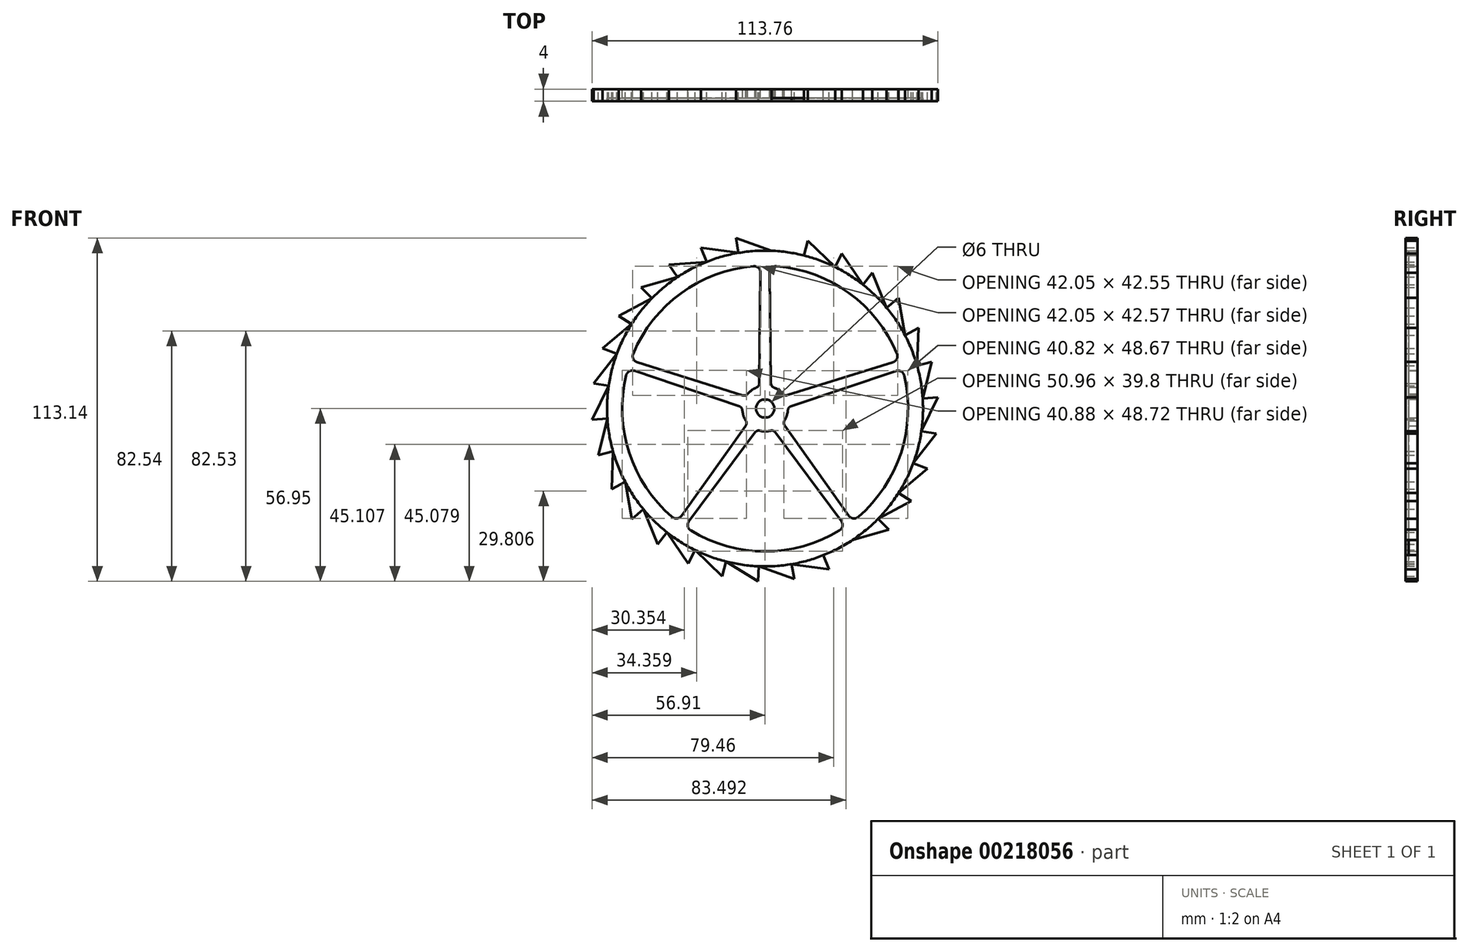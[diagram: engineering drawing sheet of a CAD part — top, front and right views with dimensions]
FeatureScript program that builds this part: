
annotation { "Feature Type Name" : "Feature", "Feature Type Description" : "" }
export const myFeature = defineFeature(function(context is Context, id is Id, definition is map)
    precondition{}
    {
        {
            var Q0;
            Q0=qCreatedBy(makeId("Front.planeOp"),FACE);
            var sketch = newSketch(context, id + "F0", { "sketchPlane" : qUnion([Q0])});
            skLineSegment(sketch, "E0", {"start": v(16.93, -54.43) * mm, "end": v(16.97, -54.42) * mm});
            skCircle(sketch, "E1", {"center": v(-0.03, 0) * mm, "radius": 52 * mm});
            skLineSegment(sketch, "E2", {"start": v(48.74, -18.05) * mm, "end": v(53.43, -19.79) * mm});
            skLineSegment(sketch, "E3", {"start": v(53.43, -19.79) * mm, "end": v(43.92, -27.8) * mm});
            skLineSegment(sketch, "E4.1.0", {"start": v(43.92, -27.8) * mm, "end": v(48.14, -30.47) * mm});
            skLineSegment(sketch, "E4.1.1", {"start": v(48.14, -30.47) * mm, "end": v(37.18, -36.33) * mm});
            skLineSegment(sketch, "E4.2.0", {"start": v(37.18, -36.33) * mm, "end": v(40.76, -39.82) * mm});
            skLineSegment(sketch, "E4.2.1", {"start": v(40.76, -39.82) * mm, "end": v(28.81, -43.27) * mm});
            skLineSegment(sketch, "E4.3.0", {"start": v(28.81, -43.27) * mm, "end": v(31.59, -47.43) * mm});
            skLineSegment(sketch, "E4.3.1", {"start": v(31.59, -47.43) * mm, "end": v(19.18, -48.32) * mm});
            skLineSegment(sketch, "E4.4.0", {"start": v(19.19, -48.32) * mm, "end": v(21.03, -52.96) * mm});
            skLineSegment(sketch, "E4.4.1", {"start": v(21.03, -52.96) * mm, "end": v(8.72, -51.26) * mm});
            skLineSegment(sketch, "E4.5.0", {"start": v(8.72, -51.26) * mm, "end": v(9.56, -56.19) * mm});
            skLineSegment(sketch, "E4.5.1", {"start": v(9.56, -56.19) * mm, "end": v(-2.13, -51.96) * mm});
            skLineSegment(sketch, "E4.6.0", {"start": v(-2.13, -51.96) * mm, "end": v(-2.33, -56.95) * mm});
            skLineSegment(sketch, "E4.6.1", {"start": v(-2.33, -56.95) * mm, "end": v(-12.89, -50.39) * mm});
            skLineSegment(sketch, "E4.7.0", {"start": v(-12.88, -50.39) * mm, "end": v(-14.12, -55.23) * mm});
            skLineSegment(sketch, "E4.7.1", {"start": v(-14.12, -55.23) * mm, "end": v(-23.08, -46.61) * mm});
            skLineSegment(sketch, "E4.8.0", {"start": v(-23.08, -46.61) * mm, "end": v(-25.3, -51.1) * mm});
            skLineSegment(sketch, "E4.8.1", {"start": v(-25.3, -51.1) * mm, "end": v(-32.27, -40.8) * mm});
            skLineSegment(sketch, "E4.9.0", {"start": v(-32.27, -40.8) * mm, "end": v(-35.37, -44.72) * mm});
            skLineSegment(sketch, "E4.9.1", {"start": v(-35.37, -44.72) * mm, "end": v(-40.05, -33.2) * mm});
            skLineSegment(sketch, "E4.10.0", {"start": v(-40.05, -33.2) * mm, "end": v(-43.9, -36.4) * mm});
            skLineSegment(sketch, "E4.10.1", {"start": v(-43.9, -36.4) * mm, "end": v(-46.08, -24.16) * mm});
            skLineSegment(sketch, "E4.11.0", {"start": v(-46.08, -24.16) * mm, "end": v(-50.5, -26.49) * mm});
            skLineSegment(sketch, "E4.11.1", {"start": v(-50.5, -26.49) * mm, "end": v(-50.1, -14.06) * mm});
            skLineSegment(sketch, "E4.12.0", {"start": v(-50.1, -14.06) * mm, "end": v(-54.9, -15.41) * mm});
            skLineSegment(sketch, "E4.12.1", {"start": v(-54.9, -15.41) * mm, "end": v(-51.92, -3.34) * mm});
            skLineSegment(sketch, "E4.13.0", {"start": v(-51.92, -3.34) * mm, "end": v(-56.91, -3.67) * mm});
            skLineSegment(sketch, "E4.13.1", {"start": v(-56.91, -3.67) * mm, "end": v(-51.48, 7.52) * mm});
            skLineSegment(sketch, "E4.14.0", {"start": v(-51.48, 7.52) * mm, "end": v(-56.43, 8.24) * mm});
            skLineSegment(sketch, "E4.14.1", {"start": v(-56.43, 8.24) * mm, "end": v(-48.8, 18.05) * mm});
            skLineSegment(sketch, "E4.15.0", {"start": v(-48.8, 18.05) * mm, "end": v(-53.49, 19.79) * mm});
            skLineSegment(sketch, "E4.15.1", {"start": v(-53.49, 19.79) * mm, "end": v(-43.98, 27.8) * mm});
            skLineSegment(sketch, "E4.16.0", {"start": v(-43.98, 27.8) * mm, "end": v(-48.2, 30.47) * mm});
            skLineSegment(sketch, "E4.16.1", {"start": v(-48.2, 30.47) * mm, "end": v(-37.24, 36.33) * mm});
            skLineSegment(sketch, "E4.17.0", {"start": v(-37.24, 36.33) * mm, "end": v(-40.82, 39.82) * mm});
            skLineSegment(sketch, "E4.17.1", {"start": v(-40.82, 39.82) * mm, "end": v(-28.87, 43.27) * mm});
            skLineSegment(sketch, "E4.18.0", {"start": v(-28.87, 43.27) * mm, "end": v(-31.65, 47.43) * mm});
            skLineSegment(sketch, "E4.18.1", {"start": v(-31.65, 47.43) * mm, "end": v(-19.24, 48.32) * mm});
            skLineSegment(sketch, "E4.19.0", {"start": v(-19.25, 48.32) * mm, "end": v(-21.1, 52.96) * mm});
            skLineSegment(sketch, "E4.19.1", {"start": v(-21.1, 52.96) * mm, "end": v(-8.78, 51.26) * mm});
            skLineSegment(sketch, "E4.20.0", {"start": v(-8.78, 51.26) * mm, "end": v(-9.62, 56.19) * mm});
            skLineSegment(sketch, "E4.20.1", {"start": v(-9.62, 56.19) * mm, "end": v(2.07, 51.96) * mm});
            skLineSegment(sketch, "E4.21.0", {"start": v(2.07, 51.96) * mm, "end": v(2.27, 56.95) * mm});
            skLineSegment(sketch, "E4.21.1", {"start": v(2.27, 56.95) * mm, "end": v(12.83, 50.39) * mm});
            skLineSegment(sketch, "E4.22.0", {"start": v(12.82, 50.39) * mm, "end": v(14.06, 55.23) * mm});
            skLineSegment(sketch, "E4.22.1", {"start": v(14.06, 55.23) * mm, "end": v(23.02, 46.61) * mm});
            skLineSegment(sketch, "E4.23.0", {"start": v(23.02, 46.61) * mm, "end": v(25.24, 51.1) * mm});
            skLineSegment(sketch, "E4.23.1", {"start": v(25.24, 51.1) * mm, "end": v(32.2, 40.8) * mm});
            skLineSegment(sketch, "E4.24.0", {"start": v(32.2, 40.8) * mm, "end": v(35.3, 44.72) * mm});
            skLineSegment(sketch, "E4.24.1", {"start": v(35.3, 44.72) * mm, "end": v(39.99, 33.2) * mm});
            skLineSegment(sketch, "E4.25.0", {"start": v(39.99, 33.2) * mm, "end": v(43.83, 36.4) * mm});
            skLineSegment(sketch, "E4.25.1", {"start": v(43.83, 36.4) * mm, "end": v(46.02, 24.16) * mm});
            skLineSegment(sketch, "E4.26.0", {"start": v(46.02, 24.16) * mm, "end": v(50.44, 26.49) * mm});
            skLineSegment(sketch, "E4.26.1", {"start": v(50.44, 26.49) * mm, "end": v(50.03, 14.06) * mm});
            skLineSegment(sketch, "E4.27.0", {"start": v(50.03, 14.06) * mm, "end": v(54.85, 15.41) * mm});
            skLineSegment(sketch, "E4.27.1", {"start": v(54.85, 15.41) * mm, "end": v(51.86, 3.34) * mm});
            skLineSegment(sketch, "E4.28.0", {"start": v(51.86, 3.34) * mm, "end": v(56.85, 3.67) * mm});
            skLineSegment(sketch, "E4.28.1", {"start": v(56.85, 3.67) * mm, "end": v(51.42, -7.52) * mm});
            skLineSegment(sketch, "E4.29.0", {"start": v(51.42, -7.52) * mm, "end": v(56.37, -8.24) * mm});
            skLineSegment(sketch, "E4.29.1", {"start": v(56.37, -8.24) * mm, "end": v(48.74, -18.05) * mm});
            skLineSegment(sketch, "E5", {"start": v(30.07, -45.16) * mm, "end": v(31.59, -47.43) * mm});
            skPoint(sketch, "E6.visualSharp", {"position": v(33.26, -42.81) * mm});
            skArc(sketch, "E6.filletArc", {"start": v(33.31, -42.89) * mm, "mid": v(33.25, -42.83) * mm, "end": v(33.17, -42.8) * mm});
            skPoint(sketch, "E7.visualSharp", {"position": v(30.65, -45.05) * mm});
            skArc(sketch, "E8", {"start": v(35.3, 44.72) * mm, "mid": v(35.3, 44.73) * mm, "end": v(35.3, 44.73) * mm});
            skLineSegment(sketch, "E9", {"start": v(32.2, 40.8) * mm, "end": v(32.2, 40.82) * mm});
            skLineSegment(sketch, "E10.trimOffspring", {"start": v(32.2, 40.8) * mm, "end": v(35.3, 44.73) * mm});
            skLineSegment(sketch, "E11", {"start": v(0, 52) * mm, "end": v(0, 52.7) * mm, "construction": true});
            skPoint(sketch, "E12.orphan", {"position": v(0, 4.97) * mm});
            skArc(sketch, "E13", {"start": v(-45.75, 10.91) * mm, "mid": v(-44.74, -14.52) * mm, "end": v(-30.63, -35.7) * mm});
            skArc(sketch, "E14", {"start": v(5.77, 4.78) * mm, "mid": v(4.43, 6.04) * mm, "end": v(2.81, 6.94) * mm});
            skLineSegment(sketch, "E15", {"start": v(0, -0.01) * mm, "end": v(0, 64.97) * mm, "construction": true});
            skLineSegment(sketch, "E16", {"start": v(62.31, 0) * mm, "end": v(-6.3, 0) * mm, "construction": true});
            skLineSegment(sketch, "E17", {"start": v(-1.52, 44.72) * mm, "end": v(-1.9, 8.35) * mm});
            skLineSegment(sketch, "E18.MirrorCS", {"start": v(1.52, 44.87) * mm, "end": v(1.9, 8.32) * mm});
            skLineSegment(sketch, "E19.1.0", {"start": v(-44.28, 15.94) * mm, "end": v(-44.25, 15.93) * mm});
            skLineSegment(sketch, "E19.1.1", {"start": v(-45.2, 13.15) * mm, "end": v(-45.16, 13.14) * mm});
            skLineSegment(sketch, "E19.2.0", {"start": v(-28.87, -37.2) * mm, "end": v(-28.84, -37.16) * mm});
            skLineSegment(sketch, "E19.2.1", {"start": v(-26.44, -38.96) * mm, "end": v(-26.42, -38.92) * mm});
            skLineSegment(sketch, "E20.2.3.0", {"start": v(26.44, -38.97) * mm, "end": v(26.41, -38.93) * mm});
            skLineSegment(sketch, "E20.3.3.0", {"start": v(28.88, -37.21) * mm, "end": v(28.84, -37.16) * mm});
            skLineSegment(sketch, "E20.2.4.0", {"start": v(45.22, 13.1) * mm, "end": v(45.17, 13.08) * mm});
            skLineSegment(sketch, "E20.3.4.0", {"start": v(42.1, 15.26) * mm, "end": v(7.35, 4.39) * mm});
            skLineSegment(sketch, "E21.trimOffspring", {"start": v(-7.5, 0) * mm, "end": v(-64.05, 0) * mm, "construction": true});
            skArc(sketch, "E22.trimOffspring", {"start": v(-2.87, 6.92) * mm, "mid": v(-4.45, 6.03) * mm, "end": v(-5.77, 4.78) * mm});
            skArc(sketch, "E23.trimOffspring", {"start": v(-7.48, -0.6) * mm, "mid": v(-7.1, -2.42) * mm, "end": v(-6.3, -4.09) * mm});
            skArc(sketch, "E24.trimOffspring", {"start": v(-1.74, -7.3) * mm, "mid": v(0.1, -7.5) * mm, "end": v(1.93, -7.26) * mm});
            skArc(sketch, "E25.trimOffspring", {"start": v(6.33, -4.03) * mm, "mid": v(7.12, -2.37) * mm, "end": v(7.48, -0.58) * mm});
            skArc(sketch, "E26.trimOffspring", {"start": v(43.41, 18.08) * mm, "mid": v(27.64, 38.04) * mm, "end": v(3.77, 46.87) * mm});
            skArc(sketch, "E27.trimOffspring", {"start": v(-3.82, 46.87) * mm, "mid": v(-27.66, 38.03) * mm, "end": v(-43.42, 18.07) * mm});
            skArc(sketch, "E28.trimOffspring", {"start": v(-24.46, -40.18) * mm, "mid": v(0, -47.04) * mm, "end": v(24.46, -40.18) * mm});
            skArc(sketch, "E29.trimOffspring", {"start": v(30.63, -35.7) * mm, "mid": v(44.73, -14.55) * mm, "end": v(45.76, 10.85) * mm});
            skArc(sketch, "E30", {"start": v(-30.63, -35.7) * mm, "mid": v(-29, -36.2) * mm, "end": v(-27.54, -35.33) * mm});
            skArc(sketch, "E31.MirrorC", {"start": v(-24.46, -40.18) * mm, "mid": v(-25.44, -38.77) * mm, "end": v(-25.06, -37.1) * mm});
            skArc(sketch, "E32.MirrorC", {"start": v(24.46, -40.18) * mm, "mid": v(25.44, -38.78) * mm, "end": v(25.06, -37.1) * mm});
            skArc(sketch, "E33.MirrorC", {"start": v(30.63, -35.7) * mm, "mid": v(29, -36.2) * mm, "end": v(27.54, -35.33) * mm});
            skArc(sketch, "E34.MirrorC", {"start": v(45.76, 10.85) * mm, "mid": v(44.73, 12.2) * mm, "end": v(43.04, 12.36) * mm});
            skArc(sketch, "E35.MirrorC", {"start": v(43.41, 18.08) * mm, "mid": v(43.38, 16.38) * mm, "end": v(42.1, 15.26) * mm});
            skPoint(sketch, "E36.endSnap0", {"position": v(22.9, 31.47) * mm});
            skArc(sketch, "E37.MirrorC", {"start": v(3.81, 46.87) * mm, "mid": v(2.15, 46.27) * mm, "end": v(1.52, 44.63) * mm});
            skArc(sketch, "E38.MirrorC", {"start": v(-3.82, 46.87) * mm, "mid": v(-2.2, 46.3) * mm, "end": v(-1.52, 44.72) * mm});
            skArc(sketch, "E39.MirrorC", {"start": v(-43.42, 18.07) * mm, "mid": v(-43.38, 16.38) * mm, "end": v(-42.1, 15.26) * mm});
            skArc(sketch, "E40.MirrorC", {"start": v(-45.75, 10.91) * mm, "mid": v(-44.72, 12.26) * mm, "end": v(-43.03, 12.42) * mm});
            skPoint(sketch, "E41.orphan", {"position": v(1.5, 47.02) * mm});
            skPoint(sketch, "E42.orphan", {"position": v(-1.5, 47.02) * mm});
            skLineSegment(sketch, "E43.trimOffspring", {"start": v(43.04, 12.36) * mm, "end": v(8.53, 0.77) * mm});
            skLineSegment(sketch, "E44.trimOffspring", {"start": v(27.54, -35.33) * mm, "end": v(6.46, -5.64) * mm});
            skLineSegment(sketch, "E45.trimOffspring", {"start": v(25.06, -37.1) * mm, "end": v(3.38, -7.87) * mm});
            skLineSegment(sketch, "E46.trimOffspring", {"start": v(-25.06, -37.1) * mm, "end": v(-3.33, -7.87) * mm});
            skLineSegment(sketch, "E47.trimOffspring", {"start": v(-27.54, -35.33) * mm, "end": v(-6.45, -5.67) * mm});
            skLineSegment(sketch, "E48.trimOffspring", {"start": v(-42.1, 15.26) * mm, "end": v(-7.36, 4.36) * mm});
            skLineSegment(sketch, "E49.trimOffspring", {"start": v(-43.03, 12.42) * mm, "end": v(-8.54, 0.75) * mm});
            skArc(sketch, "E50", {"start": v(-7.48, -0.6) * mm, "mid": v(-7.8, 0.23) * mm, "end": v(-8.54, 0.75) * mm});
            skArc(sketch, "E51.MirrorCS", {"start": v(2.81, 6.94) * mm, "mid": v(2.16, 7.5) * mm, "end": v(1.9, 8.32) * mm});
            skArc(sketch, "E52.MirrorCS", {"start": v(-1.74, -7.3) * mm, "mid": v(-2.62, -7.35) * mm, "end": v(-3.33, -7.87) * mm});
            skArc(sketch, "E53.MirrorCS", {"start": v(-5.77, 4.78) * mm, "mid": v(-6.5, 4.35) * mm, "end": v(-7.36, 4.36) * mm});
            skArc(sketch, "E54.MirrorCS", {"start": v(-2.87, 6.92) * mm, "mid": v(-2.17, 7.49) * mm, "end": v(-1.9, 8.35) * mm});
            skArc(sketch, "E55.MirrorCS", {"start": v(5.77, 4.78) * mm, "mid": v(6.5, 4.36) * mm, "end": v(7.35, 4.39) * mm});
            skArc(sketch, "E56.MirrorCS", {"start": v(7.48, -0.58) * mm, "mid": v(7.8, 0.25) * mm, "end": v(8.53, 0.77) * mm});
            skArc(sketch, "E57.MirrorCS", {"start": v(6.33, -4.03) * mm, "mid": v(6.17, -4.85) * mm, "end": v(6.46, -5.64) * mm});
            skArc(sketch, "E58.MirrorCS", {"start": v(1.93, -7.26) * mm, "mid": v(2.74, -7.37) * mm, "end": v(3.38, -7.87) * mm});
            skArc(sketch, "E59.trimOffspring", {"start": v(-6.3, -4.09) * mm, "mid": v(-6.12, -4.9) * mm, "end": v(-6.45, -5.67) * mm});
            skCircle(sketch, "E60", {"center": v(0, 0) * mm, "radius": 3 * mm});
            skCircle(sketch, "E61", {"center": v(0, 0) * mm, "radius": 7.32 * mm, "construction": true});
            skSolve(sketch);
        }
        {
            var Q0;
            {var subQ0=sQuery(id+"F0.wireOp",EDGE,"E3");var subQ1=sQuery(id+"F0.wireOp",EDGE,"E1");var subQ2=makeQuery(id+"F0.imprint","INTERSECT",VERTEX,{"derivedFrom":[subQ1,subQ0]});Q0=makeQuery(id+"F0.imprint","IMPRINT",FACE,{"disambiguationData":[TD([[makeQuery(id+"F0.imprint","IMPRINT",EDGE,{"disambiguationData":[TD([[subQ2,1.0]])],"derivedFrom":subQ1}),-1.0]])]});}
            var Q1;
            {var subQ5=sQuery(id+"F0.wireOp",EDGE,"E4.7.1");var subQ7=sQuery(id+"F0.wireOp",EDGE,"E1");var subQ8=makeQuery(id+"F0.imprint","INTERSECT",VERTEX,{"derivedFrom":[subQ7,subQ5]});Q1=makeQuery(id+"F0.imprint","IMPRINT",FACE,{"disambiguationData":[TD([[makeQuery(id+"F0.imprint","IMPRINT",EDGE,{"disambiguationData":[TD([[subQ8,1.0]])],"derivedFrom":subQ7}),-1.0]])]});}
            var Q2;
            {var subQ0=sQuery(id+"F0.wireOp",EDGE,"E5");Q2=makeQuery(id+"F0.imprint","IMPRINT",FACE,{"disambiguationData":[TD([[makeQuery(id+"F0.imprint","IMPRINT",EDGE,{"derivedFrom":subQ0}),-1.0]])]});}
            var Q3;
            {var subQ5=sQuery(id+"F0.wireOp",EDGE,"E4.6.1");var subQ7=sQuery(id+"F0.wireOp",EDGE,"E1");var subQ8=makeQuery(id+"F0.imprint","INTERSECT",VERTEX,{"derivedFrom":[subQ7,subQ5]});Q3=makeQuery(id+"F0.imprint","IMPRINT",FACE,{"disambiguationData":[TD([[makeQuery(id+"F0.imprint","IMPRINT",EDGE,{"disambiguationData":[TD([[subQ8,1.0]])],"derivedFrom":subQ7}),-1.0]])]});}
            var Q4;
            {var subQ5=sQuery(id+"F0.wireOp",EDGE,"E4.8.1");var subQ7=sQuery(id+"F0.wireOp",EDGE,"E1");var subQ8=makeQuery(id+"F0.imprint","INTERSECT",VERTEX,{"derivedFrom":[subQ7,subQ5]});Q4=makeQuery(id+"F0.imprint","IMPRINT",FACE,{"disambiguationData":[TD([[makeQuery(id+"F0.imprint","IMPRINT",EDGE,{"disambiguationData":[TD([[subQ8,1.0]])],"derivedFrom":subQ7}),-1.0]])]});}
            var Q5;
            Q5=makeQuery(id+"F0.imprint","IMPRINT",FACE,{"disambiguationData":[TD([[makeQuery(id+"F0.imprint","IMPRINT",EDGE,{"derivedFrom":sQuery(id+"F0.wireOp",EDGE,"0JxGPQ6e-XImq-FmWg-kSY9-UkRHO6Z8Cn6o")}),-1.0]])]});
            var Q6;
            {var subQ5=sQuery(id+"F0.wireOp",EDGE,"E4.4.1");var subQ7=sQuery(id+"F0.wireOp",EDGE,"E1");var subQ8=makeQuery(id+"F0.imprint","INTERSECT",VERTEX,{"derivedFrom":[subQ7,subQ5]});Q6=makeQuery(id+"F0.imprint","IMPRINT",FACE,{"disambiguationData":[TD([[makeQuery(id+"F0.imprint","IMPRINT",EDGE,{"disambiguationData":[TD([[subQ8,1.0]])],"derivedFrom":subQ7}),-1.0]])]});}
            var Q7;
            {var subQ0=sQuery(id+"F0.wireOp",EDGE,"E4.5.1");var subQ1=sQuery(id+"F0.wireOp",EDGE,"E1");var subQ2=makeQuery(id+"F0.imprint","INTERSECT",VERTEX,{"derivedFrom":[subQ1,subQ0]});Q7=makeQuery(id+"F0.imprint","IMPRINT",FACE,{"disambiguationData":[TD([[makeQuery(id+"F0.imprint","IMPRINT",EDGE,{"disambiguationData":[TD([[subQ2,1.0]])],"derivedFrom":subQ1}),-1.0]])]});}
            var Q8;
            {var subQ0=sQuery(id+"F0.wireOp",EDGE,"E4.3.1");var subQ1=sQuery(id+"F0.wireOp",EDGE,"E1");var subQ2=makeQuery(id+"F0.imprint","INTERSECT",VERTEX,{"derivedFrom":[subQ1,subQ0]});Q8=makeQuery(id+"F0.imprint","IMPRINT",FACE,{"disambiguationData":[TD([[makeQuery(id+"F0.imprint","IMPRINT",EDGE,{"disambiguationData":[TD([[subQ2,1.0]])],"derivedFrom":subQ1}),-1.0]])]});}
            var Q9;
            {var subQ5=sQuery(id+"F0.wireOp",EDGE,"E4.1.1");var subQ7=sQuery(id+"F0.wireOp",EDGE,"E1");var subQ8=makeQuery(id+"F0.imprint","INTERSECT",VERTEX,{"derivedFrom":[subQ7,subQ5]});Q9=makeQuery(id+"F0.imprint","IMPRINT",FACE,{"disambiguationData":[TD([[makeQuery(id+"F0.imprint","IMPRINT",EDGE,{"disambiguationData":[TD([[subQ8,1.0]])],"derivedFrom":subQ7}),-1.0]])]});}
            var Q10;
            {var subQ0=sQuery(id+"F0.wireOp",EDGE,"E4.4.1");var subQ1=sQuery(id+"F0.wireOp",EDGE,"E1");var subQ2=makeQuery(id+"F0.imprint","INTERSECT",VERTEX,{"derivedFrom":[subQ1,subQ0]});Q10=makeQuery(id+"F0.imprint","IMPRINT",FACE,{"disambiguationData":[TD([[makeQuery(id+"F0.imprint","IMPRINT",EDGE,{"disambiguationData":[TD([[subQ2,-1.0]])],"derivedFrom":subQ1}),-1.0]])]});}
            var Q11;
            {var subQ0=sQuery(id+"F0.wireOp",EDGE,"E4.1.1");var subQ1=sQuery(id+"F0.wireOp",EDGE,"E1");var subQ2=makeQuery(id+"F0.imprint","INTERSECT",VERTEX,{"derivedFrom":[subQ1,subQ0]});Q11=makeQuery(id+"F0.imprint","IMPRINT",FACE,{"disambiguationData":[TD([[makeQuery(id+"F0.imprint","IMPRINT",EDGE,{"disambiguationData":[TD([[subQ2,-1.0]])],"derivedFrom":subQ1}),-1.0]])]});}
            var Q12;
            {var subQ0=sQuery(id+"F0.wireOp",EDGE,"E4.3.1");var subQ1=sQuery(id+"F0.wireOp",EDGE,"E1");var subQ2=makeQuery(id+"F0.imprint","INTERSECT",VERTEX,{"derivedFrom":[subQ1,subQ0]});Q12=makeQuery(id+"F0.imprint","IMPRINT",FACE,{"disambiguationData":[TD([[makeQuery(id+"F0.imprint","IMPRINT",EDGE,{"disambiguationData":[TD([[subQ2,-1.0]])],"derivedFrom":subQ1}),-1.0]])]});}
            var Q13;
            {var subQ0=sQuery(id+"F0.wireOp",EDGE,"E4.5.1");var subQ1=sQuery(id+"F0.wireOp",EDGE,"E1");var subQ2=makeQuery(id+"F0.imprint","INTERSECT",VERTEX,{"derivedFrom":[subQ1,subQ0]});Q13=makeQuery(id+"F0.imprint","IMPRINT",FACE,{"disambiguationData":[TD([[makeQuery(id+"F0.imprint","IMPRINT",EDGE,{"disambiguationData":[TD([[subQ2,-1.0]])],"derivedFrom":subQ1}),-1.0]])]});}
            var Q14;
            {var subQ0=sQuery(id+"F0.wireOp",EDGE,"E4.6.1");var subQ1=sQuery(id+"F0.wireOp",EDGE,"E1");var subQ2=makeQuery(id+"F0.imprint","INTERSECT",VERTEX,{"derivedFrom":[subQ1,subQ0]});Q14=makeQuery(id+"F0.imprint","IMPRINT",FACE,{"disambiguationData":[TD([[makeQuery(id+"F0.imprint","IMPRINT",EDGE,{"disambiguationData":[TD([[subQ2,-1.0]])],"derivedFrom":subQ1}),-1.0]])]});}
            var Q15;
            {var subQ0=sQuery(id+"F0.wireOp",EDGE,"E4.8.1");var subQ1=sQuery(id+"F0.wireOp",EDGE,"E1");var subQ2=makeQuery(id+"F0.imprint","INTERSECT",VERTEX,{"derivedFrom":[subQ1,subQ0]});Q15=makeQuery(id+"F0.imprint","IMPRINT",FACE,{"disambiguationData":[TD([[makeQuery(id+"F0.imprint","IMPRINT",EDGE,{"disambiguationData":[TD([[subQ2,-1.0]])],"derivedFrom":subQ1}),-1.0]])]});}
            var Q16;
            {var subQ0=sQuery(id+"F0.wireOp",EDGE,"E4.7.1");var subQ1=sQuery(id+"F0.wireOp",EDGE,"E1");var subQ2=makeQuery(id+"F0.imprint","INTERSECT",VERTEX,{"derivedFrom":[subQ1,subQ0]});Q16=makeQuery(id+"F0.imprint","IMPRINT",FACE,{"disambiguationData":[TD([[makeQuery(id+"F0.imprint","IMPRINT",EDGE,{"disambiguationData":[TD([[subQ2,-1.0]])],"derivedFrom":subQ1}),-1.0]])]});}
            var Q17;
            {var subQ0=sQuery(id+"F0.wireOp",EDGE,"E4.2.1");var subQ1=sQuery(id+"F0.wireOp",EDGE,"E1");var subQ2=makeQuery(id+"F0.imprint","INTERSECT",VERTEX,{"derivedFrom":[subQ1,subQ0]});Q17=makeQuery(id+"F0.imprint","IMPRINT",FACE,{"disambiguationData":[TD([[makeQuery(id+"F0.imprint","IMPRINT",EDGE,{"disambiguationData":[TD([[subQ2,-1.0]])],"derivedFrom":subQ1}),-1.0]])]});}
            var Q18;
            {var subQ5=sQuery(id+"F0.wireOp",EDGE,"E4.25.1");var subQ7=sQuery(id+"F0.wireOp",EDGE,"E1");var subQ8=makeQuery(id+"F0.imprint","INTERSECT",VERTEX,{"derivedFrom":[subQ7,subQ5]});Q18=makeQuery(id+"F0.imprint","IMPRINT",FACE,{"disambiguationData":[TD([[makeQuery(id+"F0.imprint","IMPRINT",EDGE,{"disambiguationData":[TD([[subQ8,1.0]])],"derivedFrom":subQ7}),-1.0]])]});}
            var Q19;
            {var subQ5=sQuery(id+"F0.wireOp",EDGE,"E4.26.1");var subQ6=sQuery(id+"F0.wireOp",EDGE,"E1");var subQ7=makeQuery(id+"F0.imprint","INTERSECT",VERTEX,{"derivedFrom":[subQ6,subQ5]});Q19=makeQuery(id+"F0.imprint","IMPRINT",FACE,{"disambiguationData":[TD([[makeQuery(id+"F0.imprint","IMPRINT",EDGE,{"disambiguationData":[TD([[subQ7,1.0]])],"derivedFrom":subQ6}),-1.0]])]});}
            var Q20;
            {var subQ5=sQuery(id+"F0.wireOp",EDGE,"E2");var subQ6=sQuery(id+"F0.wireOp",EDGE,"E1");var subQ7=makeQuery(id+"F0.imprint","INTERSECT",VERTEX,{"derivedFrom":[subQ6,subQ5]});Q20=makeQuery(id+"F0.imprint","IMPRINT",FACE,{"disambiguationData":[TD([[makeQuery(id+"F0.imprint","IMPRINT",EDGE,{"disambiguationData":[TD([[subQ7,-1.0]])],"derivedFrom":subQ6}),-1.0]])]});}
            var Q21;
            {var subQ5=sQuery(id+"F0.wireOp",EDGE,"E4.24.1");var subQ7=sQuery(id+"F0.wireOp",EDGE,"E1");var subQ8=makeQuery(id+"F0.imprint","INTERSECT",VERTEX,{"derivedFrom":[subQ7,subQ5]});Q21=makeQuery(id+"F0.imprint","IMPRINT",FACE,{"disambiguationData":[TD([[makeQuery(id+"F0.imprint","IMPRINT",EDGE,{"disambiguationData":[TD([[subQ8,1.0]])],"derivedFrom":subQ7}),-1.0]])]});}
            var Q22;
            {var subQ5=sQuery(id+"F0.wireOp",EDGE,"E4.16.1");var subQ7=sQuery(id+"F0.wireOp",EDGE,"E1");var subQ8=makeQuery(id+"F0.imprint","INTERSECT",VERTEX,{"derivedFrom":[subQ7,subQ5]});Q22=makeQuery(id+"F0.imprint","IMPRINT",FACE,{"disambiguationData":[TD([[makeQuery(id+"F0.imprint","IMPRINT",EDGE,{"disambiguationData":[TD([[subQ8,1.0]])],"derivedFrom":subQ7}),-1.0]])]});}
            var Q23;
            {var subQ5=sQuery(id+"F0.wireOp",EDGE,"E4.15.1");var subQ7=sQuery(id+"F0.wireOp",EDGE,"E1");var subQ8=makeQuery(id+"F0.imprint","INTERSECT",VERTEX,{"derivedFrom":[subQ7,subQ5]});Q23=makeQuery(id+"F0.imprint","IMPRINT",FACE,{"disambiguationData":[TD([[makeQuery(id+"F0.imprint","IMPRINT",EDGE,{"disambiguationData":[TD([[subQ8,1.0]])],"derivedFrom":subQ7}),-1.0]])]});}
            var Q24;
            {var subQ0=sQuery(id+"F0.wireOp",EDGE,"E4.25.0");var subQ1=sQuery(id+"F0.wireOp",EDGE,"E1");var subQ2=makeQuery(id+"F0.imprint","INTERSECT",VERTEX,{"derivedFrom":[subQ1,subQ0]});Q24=makeQuery(id+"F0.imprint","IMPRINT",FACE,{"disambiguationData":[TD([[makeQuery(id+"F0.imprint","IMPRINT",EDGE,{"disambiguationData":[TD([[subQ2,-1.0]])],"derivedFrom":subQ0}),1.0]])]});}
            var Q25;
            {var subQ5=sQuery(id+"F0.wireOp",EDGE,"E4.22.1");var subQ7=sQuery(id+"F0.wireOp",EDGE,"E1");var subQ8=makeQuery(id+"F0.imprint","INTERSECT",VERTEX,{"derivedFrom":[subQ7,subQ5]});Q25=makeQuery(id+"F0.imprint","IMPRINT",FACE,{"disambiguationData":[TD([[makeQuery(id+"F0.imprint","IMPRINT",EDGE,{"disambiguationData":[TD([[subQ8,1.0]])],"derivedFrom":subQ7}),-1.0]])]});}
            var Q26;
            {var subQ0=sQuery(id+"F0.wireOp",EDGE,"E4.1.0");var subQ1=sQuery(id+"F0.wireOp",EDGE,"E1");var subQ2=makeQuery(id+"F0.imprint","INTERSECT",VERTEX,{"derivedFrom":[subQ1,subQ0]});Q26=makeQuery(id+"F0.imprint","IMPRINT",FACE,{"disambiguationData":[TD([[makeQuery(id+"F0.imprint","IMPRINT",EDGE,{"disambiguationData":[TD([[subQ2,-1.0]])],"derivedFrom":subQ1}),-1.0]])]});}
            var Q27;
            {var subQ5=sQuery(id+"F0.wireOp",EDGE,"E4.12.1");var subQ7=sQuery(id+"F0.wireOp",EDGE,"E1");var subQ8=makeQuery(id+"F0.imprint","INTERSECT",VERTEX,{"derivedFrom":[subQ7,subQ5]});Q27=makeQuery(id+"F0.imprint","IMPRINT",FACE,{"disambiguationData":[TD([[makeQuery(id+"F0.imprint","IMPRINT",EDGE,{"disambiguationData":[TD([[subQ8,1.0]])],"derivedFrom":subQ7}),-1.0]])]});}
            var Q28;
            {var subQ3=sQuery(id+"F0.wireOp",EDGE,"9a2ef11d-3407-4a04-9bae-d07806a6d0d6.trimOffspring");Q28=makeQuery(id+"F0.imprint","IMPRINT",FACE,{"disambiguationData":[TD([[makeQuery(id+"F0.imprint","IMPRINT",EDGE,{"derivedFrom":subQ3}),1.0]])]});}
            var Q29;
            {var subQ5=sQuery(id+"F0.wireOp",EDGE,"E4.17.1");var subQ7=sQuery(id+"F0.wireOp",EDGE,"E1");var subQ8=makeQuery(id+"F0.imprint","INTERSECT",VERTEX,{"derivedFrom":[subQ7,subQ5]});Q29=makeQuery(id+"F0.imprint","IMPRINT",FACE,{"disambiguationData":[TD([[makeQuery(id+"F0.imprint","IMPRINT",EDGE,{"disambiguationData":[TD([[subQ8,1.0]])],"derivedFrom":subQ7}),-1.0]])]});}
            var Q30;
            {var subQ5=sQuery(id+"F0.wireOp",EDGE,"E4.13.1");var subQ7=sQuery(id+"F0.wireOp",EDGE,"E1");var subQ8=makeQuery(id+"F0.imprint","INTERSECT",VERTEX,{"derivedFrom":[subQ7,subQ5]});Q30=makeQuery(id+"F0.imprint","IMPRINT",FACE,{"disambiguationData":[TD([[makeQuery(id+"F0.imprint","IMPRINT",EDGE,{"disambiguationData":[TD([[subQ8,1.0]])],"derivedFrom":subQ7}),-1.0]])]});}
            var Q31;
            {var subQ5=sQuery(id+"F0.wireOp",EDGE,"E4.27.1");var subQ7=sQuery(id+"F0.wireOp",EDGE,"E1");var subQ8=makeQuery(id+"F0.imprint","INTERSECT",VERTEX,{"derivedFrom":[subQ7,subQ5]});Q31=makeQuery(id+"F0.imprint","IMPRINT",FACE,{"disambiguationData":[TD([[makeQuery(id+"F0.imprint","IMPRINT",EDGE,{"disambiguationData":[TD([[subQ8,1.0]])],"derivedFrom":subQ7}),-1.0]])]});}
            var Q32;
            {var subQ5=sQuery(id+"F0.wireOp",EDGE,"E4.21.1");var subQ7=sQuery(id+"F0.wireOp",EDGE,"E1");var subQ8=makeQuery(id+"F0.imprint","INTERSECT",VERTEX,{"derivedFrom":[subQ7,subQ5]});Q32=makeQuery(id+"F0.imprint","IMPRINT",FACE,{"disambiguationData":[TD([[makeQuery(id+"F0.imprint","IMPRINT",EDGE,{"disambiguationData":[TD([[subQ8,1.0]])],"derivedFrom":subQ7}),-1.0]])]});}
            var Q33;
            {var subQ5=sQuery(id+"F0.wireOp",EDGE,"E4.9.1");var subQ7=sQuery(id+"F0.wireOp",EDGE,"E1");var subQ8=makeQuery(id+"F0.imprint","INTERSECT",VERTEX,{"derivedFrom":[subQ7,subQ5]});Q33=makeQuery(id+"F0.imprint","IMPRINT",FACE,{"disambiguationData":[TD([[makeQuery(id+"F0.imprint","IMPRINT",EDGE,{"disambiguationData":[TD([[subQ8,1.0]])],"derivedFrom":subQ7}),-1.0]])]});}
            var Q34;
            {var subQ5=sQuery(id+"F0.wireOp",EDGE,"E4.18.1");var subQ7=sQuery(id+"F0.wireOp",EDGE,"E1");var subQ8=makeQuery(id+"F0.imprint","INTERSECT",VERTEX,{"derivedFrom":[subQ7,subQ5]});Q34=makeQuery(id+"F0.imprint","IMPRINT",FACE,{"disambiguationData":[TD([[makeQuery(id+"F0.imprint","IMPRINT",EDGE,{"disambiguationData":[TD([[subQ8,1.0]])],"derivedFrom":subQ7}),-1.0]])]});}
            var Q35;
            {var subQ5=sQuery(id+"F0.wireOp",EDGE,"E4.10.1");var subQ7=sQuery(id+"F0.wireOp",EDGE,"E1");var subQ8=makeQuery(id+"F0.imprint","INTERSECT",VERTEX,{"derivedFrom":[subQ7,subQ5]});Q35=makeQuery(id+"F0.imprint","IMPRINT",FACE,{"disambiguationData":[TD([[makeQuery(id+"F0.imprint","IMPRINT",EDGE,{"disambiguationData":[TD([[subQ8,1.0]])],"derivedFrom":subQ7}),-1.0]])]});}
            var Q36;
            {var subQ5=sQuery(id+"F0.wireOp",EDGE,"E4.14.1");var subQ7=sQuery(id+"F0.wireOp",EDGE,"E1");var subQ8=makeQuery(id+"F0.imprint","INTERSECT",VERTEX,{"derivedFrom":[subQ7,subQ5]});Q36=makeQuery(id+"F0.imprint","IMPRINT",FACE,{"disambiguationData":[TD([[makeQuery(id+"F0.imprint","IMPRINT",EDGE,{"disambiguationData":[TD([[subQ8,1.0]])],"derivedFrom":subQ7}),-1.0]])]});}
            var Q37;
            {var subQ0=sQuery(id+"F0.wireOp",EDGE,"E4.11.1");var subQ1=sQuery(id+"F0.wireOp",EDGE,"E1");var subQ2=makeQuery(id+"F0.imprint","INTERSECT",VERTEX,{"derivedFrom":[subQ1,subQ0]});Q37=makeQuery(id+"F0.imprint","IMPRINT",FACE,{"disambiguationData":[TD([[makeQuery(id+"F0.imprint","IMPRINT",EDGE,{"disambiguationData":[TD([[subQ2,1.0]])],"derivedFrom":subQ1}),-1.0]])]});}
            var Q38;
            {var subQ0=sQuery(id+"F0.wireOp",EDGE,"E4.19.1");var subQ1=sQuery(id+"F0.wireOp",EDGE,"E1");var subQ2=makeQuery(id+"F0.imprint","INTERSECT",VERTEX,{"derivedFrom":[subQ1,subQ0]});Q38=makeQuery(id+"F0.imprint","IMPRINT",FACE,{"disambiguationData":[TD([[makeQuery(id+"F0.imprint","IMPRINT",EDGE,{"disambiguationData":[TD([[subQ2,1.0]])],"derivedFrom":subQ1}),-1.0]])]});}
            var Q39;
            {var subQ0=sQuery(id+"F0.wireOp",EDGE,"E4.12.1");var subQ1=sQuery(id+"F0.wireOp",EDGE,"E1");var subQ2=makeQuery(id+"F0.imprint","INTERSECT",VERTEX,{"derivedFrom":[subQ1,subQ0]});Q39=makeQuery(id+"F0.imprint","IMPRINT",FACE,{"disambiguationData":[TD([[makeQuery(id+"F0.imprint","IMPRINT",EDGE,{"disambiguationData":[TD([[subQ2,-1.0]])],"derivedFrom":subQ1}),-1.0]])]});}
            var Q40;
            {var subQ0=sQuery(id+"F0.wireOp",EDGE,"E4.20.1");var subQ1=sQuery(id+"F0.wireOp",EDGE,"E1");var subQ2=makeQuery(id+"F0.imprint","INTERSECT",VERTEX,{"derivedFrom":[subQ1,subQ0]});Q40=makeQuery(id+"F0.imprint","IMPRINT",FACE,{"disambiguationData":[TD([[makeQuery(id+"F0.imprint","IMPRINT",EDGE,{"disambiguationData":[TD([[subQ2,-1.0]])],"derivedFrom":subQ1}),-1.0]])]});}
            var Q41;
            {var subQ3=sQuery(id+"F0.wireOp",EDGE,"9a2ef11d-3407-4a04-9bae-d07806a6d0d6.trimOffspring");Q41=makeQuery(id+"F0.imprint","IMPRINT",FACE,{"disambiguationData":[TD([[makeQuery(id+"F0.imprint","IMPRINT",EDGE,{"derivedFrom":subQ3}),-1.0]])]});}
            var Q42;
            {var subQ0=sQuery(id+"F0.wireOp",EDGE,"E4.25.1");var subQ1=sQuery(id+"F0.wireOp",EDGE,"E1");var subQ2=makeQuery(id+"F0.imprint","INTERSECT",VERTEX,{"derivedFrom":[subQ1,subQ0]});Q42=makeQuery(id+"F0.imprint","IMPRINT",FACE,{"disambiguationData":[TD([[makeQuery(id+"F0.imprint","IMPRINT",EDGE,{"disambiguationData":[TD([[subQ2,-1.0]])],"derivedFrom":subQ1}),-1.0]])]});}
            var Q43;
            {var subQ0=sQuery(id+"F0.wireOp",EDGE,"E4.24.1");var subQ1=sQuery(id+"F0.wireOp",EDGE,"E1");var subQ2=makeQuery(id+"F0.imprint","INTERSECT",VERTEX,{"derivedFrom":[subQ1,subQ0]});Q43=makeQuery(id+"F0.imprint","IMPRINT",FACE,{"disambiguationData":[TD([[makeQuery(id+"F0.imprint","IMPRINT",EDGE,{"disambiguationData":[TD([[subQ2,-1.0]])],"derivedFrom":subQ1}),-1.0]])]});}
            var Q44;
            {var subQ0=sQuery(id+"F0.wireOp",EDGE,"E4.26.1");var subQ1=sQuery(id+"F0.wireOp",EDGE,"E1");var subQ2=makeQuery(id+"F0.imprint","INTERSECT",VERTEX,{"derivedFrom":[subQ1,subQ0]});Q44=makeQuery(id+"F0.imprint","IMPRINT",FACE,{"disambiguationData":[TD([[makeQuery(id+"F0.imprint","IMPRINT",EDGE,{"disambiguationData":[TD([[subQ2,-1.0]])],"derivedFrom":subQ1}),-1.0]])]});}
            var Q45;
            {var subQ0=sQuery(id+"F0.wireOp",EDGE,"E4.27.1");var subQ1=sQuery(id+"F0.wireOp",EDGE,"E1");var subQ2=makeQuery(id+"F0.imprint","INTERSECT",VERTEX,{"derivedFrom":[subQ1,subQ0]});Q45=makeQuery(id+"F0.imprint","IMPRINT",FACE,{"disambiguationData":[TD([[makeQuery(id+"F0.imprint","IMPRINT",EDGE,{"disambiguationData":[TD([[subQ2,-1.0]])],"derivedFrom":subQ1}),-1.0]])]});}
            var Q46;
            {var subQ0=sQuery(id+"F0.wireOp",EDGE,"E4.9.1");var subQ1=sQuery(id+"F0.wireOp",EDGE,"E1");var subQ2=makeQuery(id+"F0.imprint","INTERSECT",VERTEX,{"derivedFrom":[subQ1,subQ0]});Q46=makeQuery(id+"F0.imprint","IMPRINT",FACE,{"disambiguationData":[TD([[makeQuery(id+"F0.imprint","IMPRINT",EDGE,{"disambiguationData":[TD([[subQ2,-1.0]])],"derivedFrom":subQ1}),-1.0]])]});}
            var Q47;
            {var subQ0=sQuery(id+"F0.wireOp",EDGE,"E2");var subQ1=sQuery(id+"F0.wireOp",EDGE,"E1");var subQ2=makeQuery(id+"F0.imprint","INTERSECT",VERTEX,{"derivedFrom":[subQ1,subQ0]});Q47=makeQuery(id+"F0.imprint","IMPRINT",FACE,{"disambiguationData":[TD([[makeQuery(id+"F0.imprint","IMPRINT",EDGE,{"disambiguationData":[TD([[subQ2,1.0]])],"derivedFrom":subQ1}),-1.0]])]});}
            var Q48;
            {var subQ0=sQuery(id+"F0.wireOp",EDGE,"E4.22.1");var subQ1=sQuery(id+"F0.wireOp",EDGE,"E1");var subQ2=makeQuery(id+"F0.imprint","INTERSECT",VERTEX,{"derivedFrom":[subQ1,subQ0]});Q48=makeQuery(id+"F0.imprint","IMPRINT",FACE,{"disambiguationData":[TD([[makeQuery(id+"F0.imprint","IMPRINT",EDGE,{"disambiguationData":[TD([[subQ2,-1.0]])],"derivedFrom":subQ1}),-1.0]])]});}
            var Q49;
            {var subQ0=sQuery(id+"F0.wireOp",EDGE,"E4.19.1");var subQ1=sQuery(id+"F0.wireOp",EDGE,"E1");var subQ2=makeQuery(id+"F0.imprint","INTERSECT",VERTEX,{"derivedFrom":[subQ1,subQ0]});Q49=makeQuery(id+"F0.imprint","IMPRINT",FACE,{"disambiguationData":[TD([[makeQuery(id+"F0.imprint","IMPRINT",EDGE,{"disambiguationData":[TD([[subQ2,-1.0]])],"derivedFrom":subQ1}),-1.0]])]});}
            var Q50;
            {var subQ0=sQuery(id+"F0.wireOp",EDGE,"E4.11.1");var subQ1=sQuery(id+"F0.wireOp",EDGE,"E1");var subQ2=makeQuery(id+"F0.imprint","INTERSECT",VERTEX,{"derivedFrom":[subQ1,subQ0]});Q50=makeQuery(id+"F0.imprint","IMPRINT",FACE,{"disambiguationData":[TD([[makeQuery(id+"F0.imprint","IMPRINT",EDGE,{"disambiguationData":[TD([[subQ2,-1.0]])],"derivedFrom":subQ1}),-1.0]])]});}
            var Q51;
            {var subQ0=sQuery(id+"F0.wireOp",EDGE,"E4.13.1");var subQ1=sQuery(id+"F0.wireOp",EDGE,"E1");var subQ2=makeQuery(id+"F0.imprint","INTERSECT",VERTEX,{"derivedFrom":[subQ1,subQ0]});Q51=makeQuery(id+"F0.imprint","IMPRINT",FACE,{"disambiguationData":[TD([[makeQuery(id+"F0.imprint","IMPRINT",EDGE,{"disambiguationData":[TD([[subQ2,-1.0]])],"derivedFrom":subQ1}),-1.0]])]});}
            var Q52;
            {var subQ0=sQuery(id+"F0.wireOp",EDGE,"E4.18.1");var subQ1=sQuery(id+"F0.wireOp",EDGE,"E1");var subQ2=makeQuery(id+"F0.imprint","INTERSECT",VERTEX,{"derivedFrom":[subQ1,subQ0]});Q52=makeQuery(id+"F0.imprint","IMPRINT",FACE,{"disambiguationData":[TD([[makeQuery(id+"F0.imprint","IMPRINT",EDGE,{"disambiguationData":[TD([[subQ2,-1.0]])],"derivedFrom":subQ1}),-1.0]])]});}
            var Q53;
            {var subQ0=sQuery(id+"F0.wireOp",EDGE,"E4.21.1");var subQ1=sQuery(id+"F0.wireOp",EDGE,"E1");var subQ2=makeQuery(id+"F0.imprint","INTERSECT",VERTEX,{"derivedFrom":[subQ1,subQ0]});Q53=makeQuery(id+"F0.imprint","IMPRINT",FACE,{"disambiguationData":[TD([[makeQuery(id+"F0.imprint","IMPRINT",EDGE,{"disambiguationData":[TD([[subQ2,-1.0]])],"derivedFrom":subQ1}),-1.0]])]});}
            var Q54;
            {var subQ0=sQuery(id+"F0.wireOp",EDGE,"E4.14.1");var subQ1=sQuery(id+"F0.wireOp",EDGE,"E1");var subQ2=makeQuery(id+"F0.imprint","INTERSECT",VERTEX,{"derivedFrom":[subQ1,subQ0]});Q54=makeQuery(id+"F0.imprint","IMPRINT",FACE,{"disambiguationData":[TD([[makeQuery(id+"F0.imprint","IMPRINT",EDGE,{"disambiguationData":[TD([[subQ2,-1.0]])],"derivedFrom":subQ1}),-1.0]])]});}
            var Q55;
            {var subQ0=sQuery(id+"F0.wireOp",EDGE,"E4.28.1");var subQ1=sQuery(id+"F0.wireOp",EDGE,"E1");var subQ2=makeQuery(id+"F0.imprint","INTERSECT",VERTEX,{"derivedFrom":[subQ1,subQ0]});Q55=makeQuery(id+"F0.imprint","IMPRINT",FACE,{"disambiguationData":[TD([[makeQuery(id+"F0.imprint","IMPRINT",EDGE,{"disambiguationData":[TD([[subQ2,-1.0]])],"derivedFrom":subQ1}),-1.0]])]});}
            var Q56;
            {var subQ0=sQuery(id+"F0.wireOp",EDGE,"E4.17.1");var subQ1=sQuery(id+"F0.wireOp",EDGE,"E1");var subQ2=makeQuery(id+"F0.imprint","INTERSECT",VERTEX,{"derivedFrom":[subQ1,subQ0]});Q56=makeQuery(id+"F0.imprint","IMPRINT",FACE,{"disambiguationData":[TD([[makeQuery(id+"F0.imprint","IMPRINT",EDGE,{"disambiguationData":[TD([[subQ2,-1.0]])],"derivedFrom":subQ1}),-1.0]])]});}
            var Q57;
            {var subQ0=sQuery(id+"F0.wireOp",EDGE,"E4.10.1");var subQ1=sQuery(id+"F0.wireOp",EDGE,"E1");var subQ2=makeQuery(id+"F0.imprint","INTERSECT",VERTEX,{"derivedFrom":[subQ1,subQ0]});Q57=makeQuery(id+"F0.imprint","IMPRINT",FACE,{"disambiguationData":[TD([[makeQuery(id+"F0.imprint","IMPRINT",EDGE,{"disambiguationData":[TD([[subQ2,-1.0]])],"derivedFrom":subQ1}),-1.0]])]});}
            var Q58;
            {var subQ0=sQuery(id+"F0.wireOp",EDGE,"E4.16.1");var subQ1=sQuery(id+"F0.wireOp",EDGE,"E1");var subQ2=makeQuery(id+"F0.imprint","INTERSECT",VERTEX,{"derivedFrom":[subQ1,subQ0]});Q58=makeQuery(id+"F0.imprint","IMPRINT",FACE,{"disambiguationData":[TD([[makeQuery(id+"F0.imprint","IMPRINT",EDGE,{"disambiguationData":[TD([[subQ2,-1.0]])],"derivedFrom":subQ1}),-1.0]])]});}
            var Q59;
            {var subQ0=sQuery(id+"F0.wireOp",EDGE,"E3");var subQ1=sQuery(id+"F0.wireOp",EDGE,"E1");var subQ2=makeQuery(id+"F0.imprint","INTERSECT",VERTEX,{"derivedFrom":[subQ1,subQ0]});Q59=makeQuery(id+"F0.imprint","IMPRINT",FACE,{"disambiguationData":[TD([[makeQuery(id+"F0.imprint","IMPRINT",EDGE,{"disambiguationData":[TD([[subQ2,-1.0]])],"derivedFrom":subQ1}),-1.0]])]});}
            var Q60;
            {var subQ0=sQuery(id+"F0.wireOp",EDGE,"E4.15.1");var subQ1=sQuery(id+"F0.wireOp",EDGE,"E1");var subQ2=makeQuery(id+"F0.imprint","INTERSECT",VERTEX,{"derivedFrom":[subQ1,subQ0]});Q60=makeQuery(id+"F0.imprint","IMPRINT",FACE,{"disambiguationData":[TD([[makeQuery(id+"F0.imprint","IMPRINT",EDGE,{"disambiguationData":[TD([[subQ2,-1.0]])],"derivedFrom":subQ1}),-1.0]])]});}
            var Q61;
            {var subQ0=sQuery(id+"F0.wireOp",EDGE,"E10.trimOffspring");var subQ1=sQuery(id+"F0.wireOp",EDGE,"E4.23.1");var subQ2=makeQuery(id+"F0.imprint","INTERSECT",VERTEX,{"derivedFrom":[subQ1,subQ0]});Q61=makeQuery(id+"F0.imprint","IMPRINT",FACE,{"disambiguationData":[TD([[makeQuery(id+"F0.imprint","IMPRINT",EDGE,{"disambiguationData":[TD([[subQ2,-1.0]])],"derivedFrom":subQ1}),1.0]])]});}
            var Q62;
            {var subQ0=sQuery(id+"F0.wireOp",EDGE,"E8");Q62=makeQuery(id+"F0.imprint","IMPRINT",FACE,{"disambiguationData":[TD([[makeQuery(id+"F0.imprint","IMPRINT",EDGE,{"derivedFrom":subQ0}),1.0]])]});}
            var Q63;
            {var subQ1=sQuery(id+"F0.wireOp",EDGE,"E1");var subQ3=sQuery(id+"F0.wireOp",EDGE,"E4.24.0");var subQ4=makeQuery(id+"F0.imprint","INTERSECT",VERTEX,{"derivedFrom":[subQ1,subQ3]});Q63=makeQuery(id+"F0.imprint","IMPRINT",FACE,{"disambiguationData":[TD([[makeQuery(id+"F0.imprint","IMPRINT",EDGE,{"disambiguationData":[TD([[subQ4,-1.0]])],"derivedFrom":subQ3}),-1.0]])]});}
            var Q64;
            {var subQ1=sQuery(id+"F0.wireOp",EDGE,"E4.23.1");var subQ3=sQuery(id+"F0.wireOp",EDGE,"E4.24.0");var subQ4=makeQuery(id+"F0.imprint","INTERSECT",VERTEX,{"derivedFrom":[subQ1,subQ3]});Q64=makeQuery(id+"F0.imprint","IMPRINT",FACE,{"disambiguationData":[TD([[makeQuery(id+"F0.imprint","IMPRINT",EDGE,{"disambiguationData":[TD([[subQ4,-1.0]])],"derivedFrom":subQ3}),-1.0]])]});}
            var Q65;
            {var subQ0=sQuery(id+"F0.wireOp",EDGE,"E4.24.0");var subQ1=sQuery(id+"F0.wireOp",EDGE,"E1");var subQ2=makeQuery(id+"F0.imprint","INTERSECT",VERTEX,{"derivedFrom":[subQ1,subQ0]});Q65=makeQuery(id+"F0.imprint","IMPRINT",FACE,{"disambiguationData":[TD([[makeQuery(id+"F0.imprint","IMPRINT",EDGE,{"disambiguationData":[TD([[subQ2,-1.0]])],"derivedFrom":subQ1}),-1.0]])]});}
            var Q66;
            {var subQ0=sQuery(id+"F0.wireOp",EDGE,"5pfTocvE-Y32Q-9t7r-lnq4-AVpZhieeHUwA");Q66=makeQuery(id+"F0.imprint","IMPRINT",FACE,{"disambiguationData":[TD([[makeQuery(id+"F0.imprint","IMPRINT",EDGE,{"derivedFrom":subQ0}),1.0]])]});}
            var Q67;
            {var subQ5=sQuery(id+"F0.wireOp",EDGE,"5pfTocvE-Y32Q-9t7r-lnq4-AVpZhieeHUwA");Q67=makeQuery(id+"F0.imprint","IMPRINT",FACE,{"disambiguationData":[TD([[makeQuery(id+"F0.imprint","IMPRINT",EDGE,{"derivedFrom":subQ5}),-1.0]])]});}
            var Q68;
            {var subQ0=sQuery(id+"F0.wireOp",EDGE,"lxnnT5MD-93ew-DWKn-tZsi-ZYyrBmYGPKlA");Q68=makeQuery(id+"F0.imprint","IMPRINT",FACE,{"disambiguationData":[TD([[makeQuery(id+"F0.imprint","IMPRINT",EDGE,{"derivedFrom":subQ0}),-1.0]])]});}
            var Q69;
            {var subQ0=sQuery(id+"F0.wireOp",EDGE,"3fbe4e8f-5a92-4af8-939c-de89f58435e6.trimOffspring");var subQ3=sQuery(id+"F0.wireOp",EDGE,"oz5BJkZW-APMW-2LQB-HqCw-tHguwMOSdmba");var subQ5=makeQuery(id+"F0.imprint","INTERSECT",VERTEX,{"derivedFrom":[subQ3,subQ0]});Q69=makeQuery(id+"F0.imprint","IMPRINT",FACE,{"disambiguationData":[TD([[makeQuery(id+"F0.imprint","IMPRINT",EDGE,{"disambiguationData":[TD([[subQ5,1.0]])],"derivedFrom":subQ3}),-1.0]])]});}
            var Q70;
            {var subQ0=sQuery(id+"F0.wireOp",EDGE,"lxnnT5MD-93ew-DWKn-tZsi-ZYyrBmYGPKlA");Q70=makeQuery(id+"F0.imprint","IMPRINT",FACE,{"disambiguationData":[TD([[makeQuery(id+"F0.imprint","IMPRINT",EDGE,{"derivedFrom":subQ0}),1.0]])]});}
            extrude(context, id + "F1", {"entities" : qUnion([Q0, Q1, Q2, Q3, Q4, Q5, Q6, Q7, Q8, Q9, Q10, Q11, Q12, Q13, Q14, Q15, Q16, Q17, Q18, Q19, Q20, Q21, Q22, Q23, Q24, Q25, Q26, Q27, Q28, Q29, Q30, Q31, Q32, Q33, Q34, Q35, Q36, Q37, Q38, Q39, Q40, Q41, Q42, Q43, Q44, Q45, Q46, Q47, Q48, Q49, Q50, Q51, Q52, Q53, Q54, Q55, Q56, Q57, Q58, Q59, Q60, Q61, Q62, Q63, Q64, Q65, Q66, Q67, Q68, Q69, Q70]), "depth" : 4 * mm});
        }
        {
            var Q0;
            {var subQ72=sQuery(id+"F0.wireOp",EDGE,"E13");Q0=makeQuery(id+"F0.imprint","IMPRINT",FACE,{"disambiguationData":[TD([[makeQuery(id+"F0.imprint","IMPRINT",EDGE,{"derivedFrom":subQ72}),-1.0]])]});}
            extrude(context, id + "F2", {"entities" : qUnion([Q0]), "operationType" : NewBodyOperationType.ADD, "depth" : 3 * mm});
        }
    });
